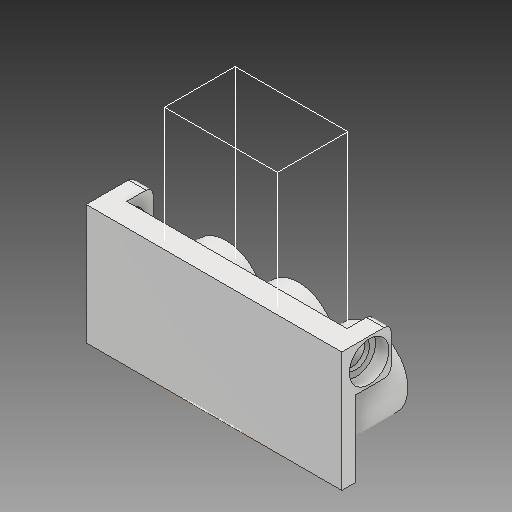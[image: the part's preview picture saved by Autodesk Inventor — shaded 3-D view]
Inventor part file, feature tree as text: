
AUTODESK INVENTOR PART (.ipt)
format: ipt  version: 2018 (Build 220112000, 112)  size: 991,744 bytes
history: native  units: mm
features: sketch x40, extrude x33, fillet x4
ambient origin geometry x8: Origin, YZ Plane, XZ Plane, XY Plane, X Axis, Y Axis, Z Axis, Center Point
bodies: Solid1 (feature_tree)
feature tree (77):
  extrude  "Extrusion1"  Depth=80.0mm
  extrude  "Extrusion2"  Depth=3.0mm
  sketch  "Sketch3"  dims[d5=12.0mm d6=14.5mm]
  extrude  "Extrusion3"  Depth=14.5mm
  extrude  "Extrusion4"  Depth=2.0mm
  extrude  "Extrusion5"  Depth=0.5mm TaperAngle=0.0deg
  sketch  "Sketch7"  dims[d15=10.0mm d16=25.0mm]
  extrude  "Extrusion6"  Depth=25.0mm
  extrude  "Extrusion7"  Depth=25.0mm
  extrude  "Extrusion8"  Depth=22.5mm
  fillet  "Fillet1"  Radius=10.0mm
  fillet  "Fillet2"  Radius=10.0mm
  extrude  "Extrusion9"  Depth=7.5mm TaperAngle=0.0deg
  extrude  "Extrusion10"  Depth=3.0mm
  fillet  "Fillet3"  Radius=3.0mm
  extrude  "Extrusion11"  Depth=21.0mm
  extrude  "Extrusion12"  Depth=41.0mm
  extrude  "Extrusion13"  Depth=42.0mm
  extrude  "Extrusion14"  Depth=38.0mm
  extrude  "Extrusion15"  Depth=42.0mm TaperAngle=0.0deg
  extrude  "Extrusion16"  Depth=3.0mm TaperAngle=0.0deg
  extrude  "Extrusion17"  Depth=3.0mm
  extrude  "Extrusion18"  Depth=39.5mm
  extrude  "Extrusion19"  Depth=7.25mm
  extrude  "Extrusion20"  Depth=125.0mm
  extrude  "Extrusion21"  Depth=1.0mm
  sketch  "Sketch24"  dims[d65=66.0mm d66=3.5mm d67=0.0mm]
  extrude  "Extrusion22"  Depth=10.0mm TaperAngle=0.0deg
  extrude  "Extrusion23"  Depth=16.0mm
  extrude  "Extrusion24"  Depth=3.5mm TaperAngle=0.0deg
  extrude  "Extrusion25"  Depth=2.0mm
  extrude  "Extrusion26"  Depth=2.0mm TaperAngle=0.0deg
  sketch  "Sketch30"  dims[d81=4.0mm d82=4.0mm]
  extrude  "Extrusion27"  Depth=16.0mm
  extrude  "Extrusion28"  Depth=2.0mm
  extrude  "Extrusion29"  Depth=3.5mm TaperAngle=0.0deg
  sketch  "Sketch34"  dims[d92=16.0mm]
  extrude  "Extrusion30"  Depth=4.0mm
  sketch  "Sketch36"  dims[d94=12.0mm]
  extrude  "Extrusion31"  Depth=2.0mm TaperAngle=0.0deg
  sketch  "Sketch38"  dims[d96=43.0mm d97=0.0mm]
  extrude  "Extrusion32"  Depth=150.0mm TaperAngle=0.0deg
  extrude  "Extrusion33"  Depth=16.0mm
  fillet  "Fillet4"  Radius=5.0mm
  sketch  "Sketch1"  dims[d0=145.0mm d1=80.0mm]
  sketch  "Sketch2"  dims[d2=3.0mm d3=0.0mm d4=12.0mm]
  sketch  "Sketch4"  dims[d7=2.0mm d8=2.0mm]
  sketch  "Sketch5"  dims[d9=6.0mm d10=0.0mm d11=0.5mm d12=0.0mm]
  sketch  "Sketch6"  dims[d13=10.0mm d14=25.0mm]
  sketch  "Sketch8"  dims[d17=25.0mm d18=0.0mm d19=22.5mm d20=10.0mm d21=0.0mm d22=10.0mm]
  sketch  "Sketch9"  dims[d23=2.5mm d24=0.0mm d25=7.5mm d26=0.0mm]
  sketch  "Sketch10"  dims[d27=10.0mm d28=0.0mm d29=4.0mm d30=3.0mm]
  sketch  "Sketch11"  dims[d31=1.0mm d32=21.0mm]
  sketch  "Sketch12"  dims[d33=38.0mm d34=41.0mm]
  sketch  "Sketch13"  dims[d35=38.0mm d36=42.0mm]
  sketch  "Sketch14"  dims[d37=41.0mm d38=38.0mm]
  sketch  "Sketch15"  dims[d39=42.0mm d40=45.0mm d41=0.0mm]
  sketch  "Sketch16"  dims[d42=12.5mm d43=3.0mm d44=0.0mm]
  sketch  "Sketch17"  dims[d45=3.0mm d46=39.5mm]
  sketch  "Sketch18"  dims[d47=39.5mm d48=39.5mm]
  sketch  "Sketch19"  dims[d49=45.0mm d50=0.0mm d51=7.25mm]
  sketch  "Sketch20"  dims[d52=4.0mm d53=7.75mm d54=0.0mm d55=0.0mm d56=125.0mm]
  sketch  "Sketch21"  dims[d57=10.0mm d58=0.0mm d59=1.0mm]
  sketch  "Sketch22"  dims[d60=14.5mm d61=10.0mm d62=0.0mm]
  sketch  "Sketch23"  dims[d63=16.0mm d64=12.0mm]
  sketch  "Sketch25"  dims[d68=4.0mm d69=2.0mm]
  sketch  "Sketch26"  dims[d70=4.0mm d71=2.0mm d72=0.0mm]
  sketch  "Sketch27"  dims[d73=2.0mm d74=0.0mm d75=16.0mm]
  sketch  "Sketch28"  dims[d76=2.0mm d77=2.0mm]
  sketch  "Sketch29"  dims[d78=2.0mm d79=3.5mm d80=0.0mm]
  sketch  "Sketch31"  dims[d83=4.0mm d84=2.0mm d85=0.0mm]
  sketch  "Sketch32"  dims[d86=15.5mm d87=150.0mm d88=0.0mm]
  sketch  "Sketch33"  dims[d89=12.0mm d90=16.0mm d91=5.0mm]
  sketch  "Sketch35"  dims[d93=5.0mm]
  sketch  "Sketch37"  dims[d95=3.0mm]
  sketch  "Sketch39"  dims[d98=43.0mm d99=0.0mm]
  sketch  "Sketch40"  dims[d100=38.75mm d101=38.75mm d102=5.0mm d103=0.0mm d104=500.0mm d105=0.0mm d106=45.0mm d107=0.0mm d108=45.0mm d109=0.0mm d110=38.75mm d111=38.75mm d112=45.0mm d113=0.0mm d114=3.5mm d115=0.0mm d116=43.0mm d117=0.0mm d118=12.25mm d119=3.5mm d120=12.25mm d121=3.5mm d122=43.0mm d123=0.0mm d124=2.0mm d125=0.0mm d126=2.5mm d127=2.5mm d128=5.0mm d129=5.0mm d130=0.0mm d131=2.5mm d132=2.5mm d133=5.0mm d134=0.0mm d135=1.0mm]
